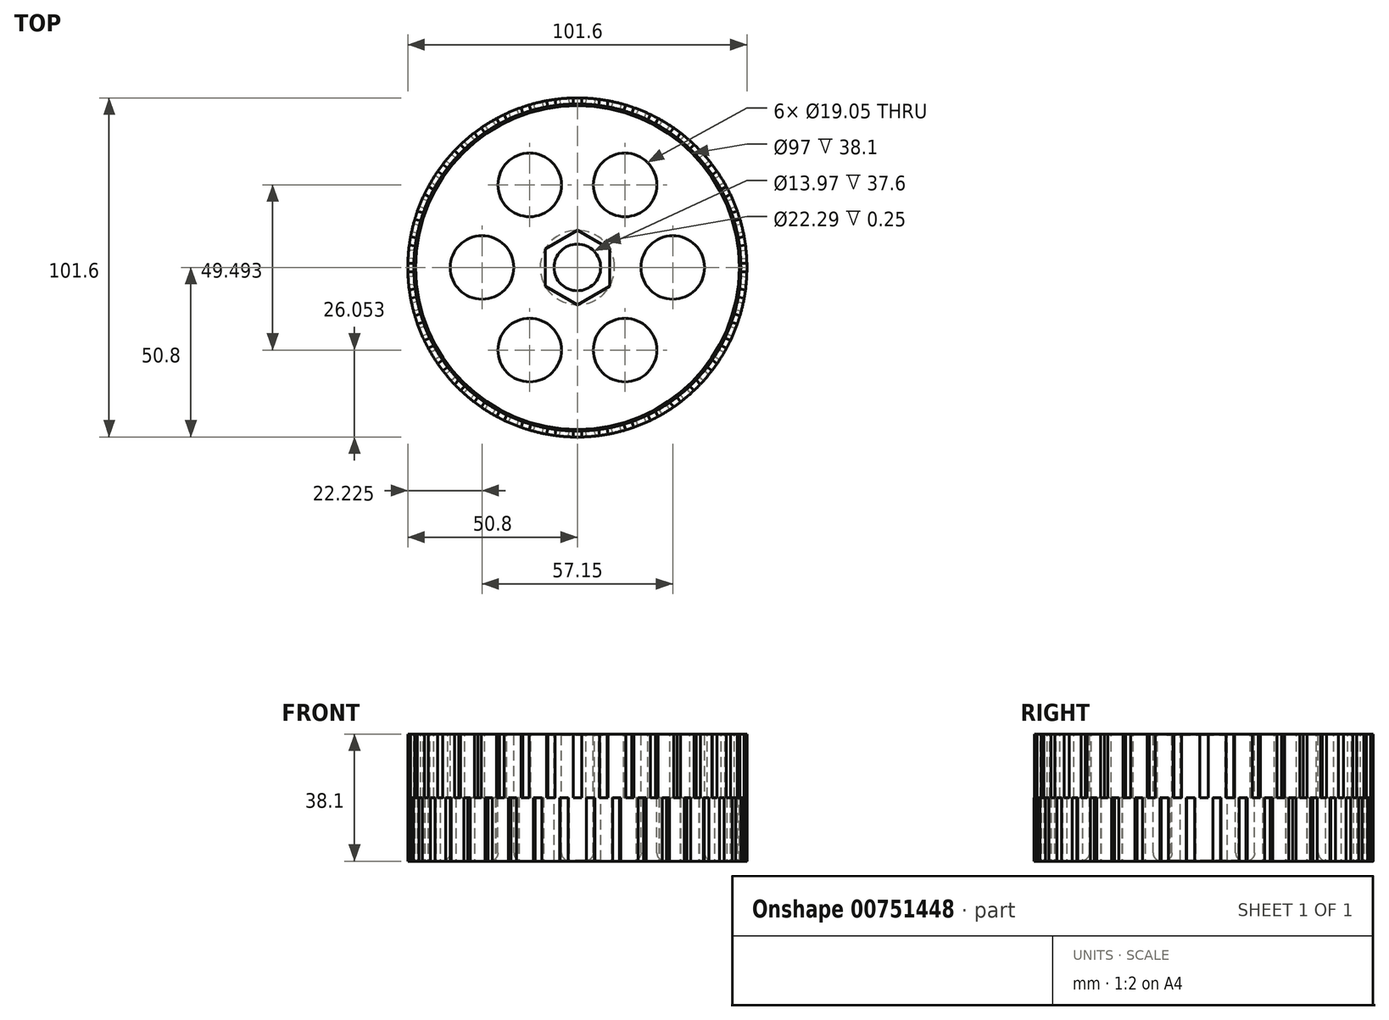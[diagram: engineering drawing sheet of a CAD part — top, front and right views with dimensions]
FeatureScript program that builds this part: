
annotation { "Feature Type Name" : "Feature", "Feature Type Description" : "" }
export const myFeature = defineFeature(function(context is Context, id is Id, definition is map)
    precondition{}
    {
        {
            assignVariable(context, id + "F0", {"name" : "BoltHeadDepth", "anyValue" : 0.25});
        }
        {
            assignVariable(context, id + "F1", {"name" : "NutDepth", "anyValue" : 0.25});
        }
        {
            var Q0;
            Q0=qCreatedBy(makeId("Front.planeOp"),FACE);
            var sketch = newSketch(context, id + "F2", { "sketchPlane" : qUnion([Q0])});
            skLineSegment(sketch, "E0.bottom", {"start": v(0, 38.1) * mm, "end": v(50.8, 38.1) * mm, "construction": true});
            skLineSegment(sketch, "E0.top", {"start": v(0, 0) * mm, "end": v(50.8, 0) * mm, "construction": true});
            skLineSegment(sketch, "E0.left", {"start": v(0, 38.1) * mm, "end": v(0, 0) * mm, "construction": true});
            skLineSegment(sketch, "E0.right", {"start": v(50.8, 38.1) * mm, "end": v(50.8, 0) * mm});
            skArc(sketch, "E1", {"start": v(49, 0) * mm, "mid": v(50.8, 19.05) * mm, "end": v(49, 38.1) * mm});
            skPoint(sketch, "E2", {"position": v(50.8, 19.05) * mm});
            skPoint(sketch, "E3", {"position": v(0, 19.05) * mm});
            skLineSegment(sketch, "E4.bottom", {"start": v(0, 38.1) * mm, "end": v(49, 38.1) * mm});
            skLineSegment(sketch, "E4.top", {"start": v(0, 0) * mm, "end": v(49, 0) * mm});
            skLineSegment(sketch, "E4.left", {"start": v(0, 38.1) * mm, "end": v(0, 0) * mm});
            skLineSegment(sketch, "E5", {"start": v(49, 38.1) * mm, "end": v(49, 0) * mm});
            skLineSegment(sketch, "E6.bottom", {"start": v(49, 38.1) * mm, "end": v(48, 38.1) * mm});
            skLineSegment(sketch, "E6.top", {"start": v(49, 0) * mm, "end": v(48, 0) * mm});
            skLineSegment(sketch, "E6.right", {"start": v(48, 38.1) * mm, "end": v(48, 0) * mm});
            skLineSegment(sketch, "E7", {"start": v(48.5, 38.1) * mm, "end": v(48.5, 0) * mm});
            skLineSegment(sketch, "E8", {"start": v(49, 38.1) * mm, "end": v(50.8, 38.1) * mm});
            skLineSegment(sketch, "E9", {"start": v(49, 0) * mm, "end": v(50.8, 0) * mm});
            skSolve(sketch);
        }
        {
            var Q0;
            Q0=makeQuery(id+"F2.imprint","IMPRINT",FACE,{"disambiguationData":[TD([[makeQuery(id+"F2.imprint","IMPRINT",EDGE,{"derivedFrom":sQuery(id+"F2.wireOp",EDGE,"E4.bottom")}),-1.0]])]});
            var Q1;
            {var subQ0=sQuery(id+"F2.wireOp",EDGE,"E6.right");Q1=makeQuery(id+"F2.imprint","IMPRINT",FACE,{"disambiguationData":[TD([[makeQuery(id+"F2.imprint","IMPRINT",EDGE,{"derivedFrom":subQ0}),1.0]])]});}
            var Q2;
            {var subQ0=sQuery(id+"F2.wireOp",EDGE,"E5");Q2=makeQuery(id+"F2.imprint","IMPRINT",FACE,{"disambiguationData":[TD([[makeQuery(id+"F2.imprint","IMPRINT",EDGE,{"derivedFrom":subQ0}),-1.0]])]});}
            var Q3;
            Q3=sQuery(id+"F2.wireOp",EDGE,"E4.left");
            revolve(context, id + "F3", {"surfaceOperationType" : NewSurfaceOperationType.NEW, "entities" : qUnion([Q0, Q1, Q2]), "axis" : qUnion([Q3]), "revolveType" : RevolveType.FULL});
        }
        {
            var Q0;
            Q0=makeQuery(id+"F2.imprint","IMPRINT",FACE,{"disambiguationData":[TD([[makeQuery(id+"F2.imprint","IMPRINT",EDGE,{"derivedFrom":sQuery(id+"F2.wireOp",EDGE,"E1")}),1.0]])]});
            var Q1;
            {var subQ0=sQuery(id+"F2.wireOp",EDGE,"E5");Q1=makeQuery(id+"F2.imprint","IMPRINT",FACE,{"disambiguationData":[TD([[makeQuery(id+"F2.imprint","IMPRINT",EDGE,{"derivedFrom":subQ0}),-1.0]])]});}
            var Q2;
            {var subQ0=sQuery(id+"F2.wireOp",EDGE,"E8");Q2=makeQuery(id+"F2.imprint","IMPRINT",FACE,{"disambiguationData":[TD([[makeQuery(id+"F2.imprint","IMPRINT",EDGE,{"derivedFrom":subQ0}),-1.0]])]});}
            var Q3;
            {var subQ0=sQuery(id+"F2.wireOp",EDGE,"E9");Q3=makeQuery(id+"F2.imprint","IMPRINT",FACE,{"disambiguationData":[TD([[makeQuery(id+"F2.imprint","IMPRINT",EDGE,{"derivedFrom":subQ0}),1.0]])]});}
            var Q4;
            Q4=sQuery(id+"F2.wireOp",EDGE,"E4.left");
            revolve(context, id + "F4", {"surfaceOperationType" : NewSurfaceOperationType.NEW, "entities" : qUnion([Q0, Q1, Q2, Q3]), "axis" : qUnion([Q4]), "revolveType" : RevolveType.FULL});
        }
        {
            var Q0;
            Q0=makeQuery(id+"F3.opRevolve","SWEPT_FACE",FACE,{"disambiguationData":[OSD([sQuery(id+"F2.wireOp",EDGE,"E4.bottom")])]});
            var sketch = newSketch(context, id + "F5", { "sketchPlane" : qUnion([Q0])});
            skCircle(sketch, "E10", {"center": v(0, 0) * mm, "radius": 6.99 * mm});
            skCircle(sketch, "E11.cCircle", {"center": v(0, 0) * mm, "radius": 9.65 * mm, "construction": true});
            skLineSegment(sketch, "E11.0", {"start": v(9.65, 5.57) * mm, "end": v(9.65, -5.57) * mm});
            skLineSegment(sketch, "E11.1", {"start": v(9.65, -5.57) * mm, "end": v(0, -11.15) * mm});
            skLineSegment(sketch, "E11.2", {"start": v(0, -11.15) * mm, "end": v(-9.65, -5.57) * mm});
            skLineSegment(sketch, "E11.3", {"start": v(-9.65, -5.57) * mm, "end": v(-9.65, 5.57) * mm});
            skLineSegment(sketch, "E11.4", {"start": v(-9.65, 5.57) * mm, "end": v(0, 11.15) * mm});
            skLineSegment(sketch, "E11.5", {"start": v(0, 11.15) * mm, "end": v(9.65, 5.57) * mm});
            skPoint(sketch, "E11.0.midPoint", {"position": v(9.65, 0) * mm});
            skSolve(sketch);
        }
        {
            var Q0;
            Q0=makeQuery(id+"F5.imprint","IMPRINT",FACE,{"disambiguationData":[TD([[makeQuery(id+"F5.imprint","IMPRINT",EDGE,{"derivedFrom":sQuery(id+"F5.wireOp",EDGE,"E10")}),1.0]])]});
            extrude(context, id + "F6", {"entities" : qUnion([Q0]), "operationType" : NewBodyOperationType.REMOVE, "endBound" : BoundingType.THROUGH_ALL, "oppositeDirection" : true, "depth" : 25.4 * mm, "offsetDistance" : 25.4 * mm});
        }
        {
            var Q0;
            Q0=makeQuery(id+"F5.imprint","IMPRINT",FACE,{"disambiguationData":[TD([[makeQuery(id+"F5.imprint","IMPRINT",EDGE,{"derivedFrom":sQuery(id+"F5.wireOp",EDGE,"E10")}),-1.0]])]});
            extrude(context, id + "F7", {"entities" : qUnion([Q0]), "operationType" : NewBodyOperationType.REMOVE, "oppositeDirection" : true, "depth" : (getVariable(context, 'BoltHeadDepth')) * mm, "offsetDistance" : 25.4 * mm});
        }
        {
            var Q0;
            Q0=makeQuery(id+"F3.opRevolve","SWEPT_FACE",FACE,{"disambiguationData":[OSD([sQuery(id+"F2.wireOp",EDGE,"E4.top")])]});
            var sketch = newSketch(context, id + "F8", { "sketchPlane" : qUnion([Q0])});
            skCircle(sketch, "E12", {"center": v(0, 0) * mm, "radius": 11.15 * mm});
            skSolve(sketch);
        }
        {
            var Q0;
            Q0=makeQuery(id+"F8.imprint","IMPRINT",FACE,{"disambiguationData":[TD([[makeQuery(id+"F8.imprint","IMPRINT",EDGE,{"derivedFrom":sQuery(id+"F8.wireOp",EDGE,"E12")}),1.0]])]});
            extrude(context, id + "F9", {"entities" : qUnion([Q0]), "operationType" : NewBodyOperationType.REMOVE, "oppositeDirection" : true, "depth" : (getVariable(context, 'NutDepth')) * mm, "offsetDistance" : 25.4 * mm});
        }
        {
            var Q0;
            Q0=makeQuery(id+"F5.imprint","IMPRINT",FACE,{"disambiguationData":[TD([[makeQuery(id+"F5.imprint","IMPRINT",EDGE,{"derivedFrom":sQuery(id+"F5.wireOp",EDGE,"E11.0")}),1.0]])]});
            var sketch = newSketch(context, id + "F10", { "sketchPlane" : qUnion([Q0])});
            skCircle(sketch, "E13", {"center": v(-28.58, 0) * mm, "radius": 9.53 * mm});
            skCircle(sketch, "E14", {"center": v(28.58, 0) * mm, "radius": 9.53 * mm});
            skCircle(sketch, "E15", {"center": v(0, 0) * mm, "radius": 28.58 * mm, "construction": true});
            skCircle(sketch, "E16.1.0", {"center": v(14.29, -24.75) * mm, "radius": 9.53 * mm});
            skCircle(sketch, "E16.1.1", {"center": v(-14.29, 24.75) * mm, "radius": 9.53 * mm});
            skCircle(sketch, "E16.2.0", {"center": v(14.29, 24.75) * mm, "radius": 9.53 * mm});
            skCircle(sketch, "E16.2.1", {"center": v(-14.29, -24.75) * mm, "radius": 9.53 * mm});
            skSolve(sketch);
        }
        {
            var Q0;
            Q0 = qSketchRegion(id + "F10", true);
            extrude(context, id + "F11", {"entities" : qUnion([Q0]), "operationType" : NewBodyOperationType.REMOVE, "endBound" : BoundingType.THROUGH_ALL, "oppositeDirection" : true, "depth" : 25.4 * mm, "offsetDistance" : 25.4 * mm});
        }
        {
            var Q0;
            Q0=makeQuery(id+"F11.boolean.opBoolean","COPY",EDGE,{"derivedFrom":makeQuery(id+"F11.opExtrude","CAP_EDGE",EDGE,{"disambiguationData":[OSD([sQuery(id+"F10.wireOp",EDGE,"E16.1.1")])],"isStart":true})});
            var Q1;
            Q1=makeQuery(id+"F11.boolean.opBoolean","COPY",EDGE,{"derivedFrom":makeQuery(id+"F11.opExtrude","CAP_EDGE",EDGE,{"disambiguationData":[OSD([sQuery(id+"F10.wireOp",EDGE,"E16.2.0")])],"isStart":true})});
            var Q2;
            Q2=makeQuery(id+"F11.boolean.opBoolean","COPY",EDGE,{"derivedFrom":makeQuery(id+"F11.opExtrude","CAP_EDGE",EDGE,{"disambiguationData":[OSD([sQuery(id+"F10.wireOp",EDGE,"E14")])],"isStart":true})});
            var Q3;
            Q3=makeQuery(id+"F11.boolean.opBoolean","COPY",EDGE,{"derivedFrom":makeQuery(id+"F11.opExtrude","CAP_EDGE",EDGE,{"disambiguationData":[OSD([sQuery(id+"F10.wireOp",EDGE,"E16.1.0")])],"isStart":true})});
            var Q4;
            Q4=makeQuery(id+"F11.boolean.opBoolean","COPY",EDGE,{"derivedFrom":makeQuery(id+"F11.opExtrude","CAP_EDGE",EDGE,{"disambiguationData":[OSD([sQuery(id+"F10.wireOp",EDGE,"E16.2.1")])],"isStart":true})});
            var Q5;
            Q5=makeQuery(id+"F11.boolean.opBoolean","COPY",EDGE,{"derivedFrom":makeQuery(id+"F11.opExtrude","CAP_EDGE",EDGE,{"disambiguationData":[OSD([sQuery(id+"F10.wireOp",EDGE,"E13")])],"isStart":true})});
            var Q6;
            Q6=makeQuery(id+"F11.boolean.opBoolean","INTERSECT",EDGE,{"derivedFrom":[makeQuery(id+"F3.opRevolve","SWEPT_FACE",FACE,{"disambiguationData":[OSD([sQuery(id+"F2.wireOp",EDGE,"E4.top"),sQuery(id+"F2.wireOp",EDGE,"E6.top")])]}),makeQuery(id+"F11.opExtrude","SWEPT_FACE",FACE,{"disambiguationData":[OSD([sQuery(id+"F10.wireOp",EDGE,"E16.1.1")])]})]});
            var Q7;
            Q7=makeQuery(id+"F11.boolean.opBoolean","INTERSECT",EDGE,{"derivedFrom":[makeQuery(id+"F3.opRevolve","SWEPT_FACE",FACE,{"disambiguationData":[OSD([sQuery(id+"F2.wireOp",EDGE,"E4.top"),sQuery(id+"F2.wireOp",EDGE,"E6.top")])]}),makeQuery(id+"F11.opExtrude","SWEPT_FACE",FACE,{"disambiguationData":[OSD([sQuery(id+"F10.wireOp",EDGE,"E13")])]})]});
            var Q8;
            Q8=makeQuery(id+"F11.boolean.opBoolean","INTERSECT",EDGE,{"derivedFrom":[makeQuery(id+"F3.opRevolve","SWEPT_FACE",FACE,{"disambiguationData":[OSD([sQuery(id+"F2.wireOp",EDGE,"E4.top"),sQuery(id+"F2.wireOp",EDGE,"E6.top")])]}),makeQuery(id+"F11.opExtrude","SWEPT_FACE",FACE,{"disambiguationData":[OSD([sQuery(id+"F10.wireOp",EDGE,"E16.2.1")])]})]});
            var Q9;
            Q9=makeQuery(id+"F11.boolean.opBoolean","INTERSECT",EDGE,{"derivedFrom":[makeQuery(id+"F3.opRevolve","SWEPT_FACE",FACE,{"disambiguationData":[OSD([sQuery(id+"F2.wireOp",EDGE,"E4.top"),sQuery(id+"F2.wireOp",EDGE,"E6.top")])]}),makeQuery(id+"F11.opExtrude","SWEPT_FACE",FACE,{"disambiguationData":[OSD([sQuery(id+"F10.wireOp",EDGE,"E16.1.0")])]})]});
            var Q10;
            Q10=makeQuery(id+"F11.boolean.opBoolean","INTERSECT",EDGE,{"derivedFrom":[makeQuery(id+"F3.opRevolve","SWEPT_FACE",FACE,{"disambiguationData":[OSD([sQuery(id+"F2.wireOp",EDGE,"E4.top"),sQuery(id+"F2.wireOp",EDGE,"E6.top")])]}),makeQuery(id+"F11.opExtrude","SWEPT_FACE",FACE,{"disambiguationData":[OSD([sQuery(id+"F10.wireOp",EDGE,"E14")])]})]});
            var Q11;
            Q11=makeQuery(id+"F11.boolean.opBoolean","INTERSECT",EDGE,{"derivedFrom":[makeQuery(id+"F3.opRevolve","SWEPT_FACE",FACE,{"disambiguationData":[OSD([sQuery(id+"F2.wireOp",EDGE,"E4.top"),sQuery(id+"F2.wireOp",EDGE,"E6.top")])]}),makeQuery(id+"F11.opExtrude","SWEPT_FACE",FACE,{"disambiguationData":[OSD([sQuery(id+"F10.wireOp",EDGE,"E16.2.0")])]})]});
            fillet(context, id + "F12", {"entities" : qUnion([Q0, Q1, Q2, Q3, Q4, Q5, Q6, Q7, Q8, Q9, Q10, Q11]), "radius" : 2.54 * mm, "tangentPropagation" : true, "allowEdgeOverflow" : false});
        }
        {
            var Q0;
            Q0=makeQuery(id+"F5.imprint","IMPRINT",FACE,{"disambiguationData":[TD([[makeQuery(id+"F5.imprint","IMPRINT",EDGE,{"derivedFrom":sQuery(id+"F5.wireOp",EDGE,"E11.0")}),1.0]])]});
            var sketch = newSketch(context, id + "F13", { "sketchPlane" : qUnion([Q0])});
            skLineSegment(sketch, "E17.bottom", {"start": v(-1.27, 51.52) * mm, "end": v(1.27, 51.52) * mm});
            skLineSegment(sketch, "E17.top", {"start": v(-1.27, 48.98) * mm, "end": v(1.27, 48.98) * mm});
            skLineSegment(sketch, "E17.left", {"start": v(-1.27, 51.52) * mm, "end": v(-1.27, 48.98) * mm});
            skLineSegment(sketch, "E17.right", {"start": v(1.27, 51.52) * mm, "end": v(1.27, 48.98) * mm});
            skPoint(sketch, "E18", {"position": v(0, 51.52) * mm});
            skPoint(sketch, "E18.positionSnap0", {"position": v(0, 51.52) * mm});
            skLineSegment(sketch, "E19.1.0", {"start": v(-6.8, 51.09) * mm, "end": v(-6.4, 48.58) * mm});
            skLineSegment(sketch, "E19.1.1", {"start": v(-9.31, 50.69) * mm, "end": v(-6.8, 51.09) * mm});
            skLineSegment(sketch, "E19.1.2", {"start": v(-9.31, 50.69) * mm, "end": v(-8.92, 48.18) * mm});
            skLineSegment(sketch, "E19.1.3", {"start": v(-8.92, 48.18) * mm, "end": v(-6.4, 48.58) * mm});
            skLineSegment(sketch, "E19.2.0", {"start": v(-14.71, 49.4) * mm, "end": v(-13.93, 46.98) * mm});
            skLineSegment(sketch, "E19.2.1", {"start": v(-17.13, 48.6) * mm, "end": v(-14.71, 49.4) * mm});
            skLineSegment(sketch, "E19.2.2", {"start": v(-17.13, 48.6) * mm, "end": v(-16.34, 46.2) * mm});
            skLineSegment(sketch, "E19.2.3", {"start": v(-16.34, 46.2) * mm, "end": v(-13.93, 46.98) * mm});
            skLineSegment(sketch, "E19.3.0", {"start": v(-22.26, 46.48) * mm, "end": v(-21.1, 44.22) * mm});
            skLineSegment(sketch, "E19.3.1", {"start": v(-24.52, 45.33) * mm, "end": v(-22.26, 46.48) * mm});
            skLineSegment(sketch, "E19.3.2", {"start": v(-24.52, 45.33) * mm, "end": v(-23.37, 43.07) * mm});
            skLineSegment(sketch, "E19.3.3", {"start": v(-23.37, 43.07) * mm, "end": v(-21.1, 44.22) * mm});
            skLineSegment(sketch, "E19.4.0", {"start": v(-29.26, 42.43) * mm, "end": v(-27.76, 40.37) * mm});
            skLineSegment(sketch, "E19.4.1", {"start": v(-31.31, 40.94) * mm, "end": v(-29.26, 42.43) * mm});
            skLineSegment(sketch, "E19.4.2", {"start": v(-31.31, 40.94) * mm, "end": v(-29.82, 38.88) * mm});
            skLineSegment(sketch, "E19.4.3", {"start": v(-29.82, 38.88) * mm, "end": v(-27.76, 40.37) * mm});
            skLineSegment(sketch, "E19.5.0", {"start": v(-35.53, 37.33) * mm, "end": v(-33.74, 35.53) * mm});
            skLineSegment(sketch, "E19.5.1", {"start": v(-37.33, 35.53) * mm, "end": v(-35.53, 37.33) * mm});
            skLineSegment(sketch, "E19.5.2", {"start": v(-37.33, 35.53) * mm, "end": v(-35.53, 33.74) * mm});
            skLineSegment(sketch, "E19.5.3", {"start": v(-35.53, 33.74) * mm, "end": v(-33.74, 35.53) * mm});
            skLineSegment(sketch, "E19.6.0", {"start": v(-40.94, 31.31) * mm, "end": v(-38.88, 29.82) * mm});
            skLineSegment(sketch, "E19.6.1", {"start": v(-42.43, 29.26) * mm, "end": v(-40.94, 31.31) * mm});
            skLineSegment(sketch, "E19.6.2", {"start": v(-42.43, 29.26) * mm, "end": v(-40.37, 27.76) * mm});
            skLineSegment(sketch, "E19.6.3", {"start": v(-40.37, 27.76) * mm, "end": v(-38.88, 29.82) * mm});
            skLineSegment(sketch, "E19.7.0", {"start": v(-45.33, 24.52) * mm, "end": v(-43.07, 23.37) * mm});
            skLineSegment(sketch, "E19.7.1", {"start": v(-46.48, 22.26) * mm, "end": v(-45.33, 24.52) * mm});
            skLineSegment(sketch, "E19.7.2", {"start": v(-46.48, 22.26) * mm, "end": v(-44.22, 21.1) * mm});
            skLineSegment(sketch, "E19.7.3", {"start": v(-44.22, 21.1) * mm, "end": v(-43.07, 23.37) * mm});
            skLineSegment(sketch, "E19.8.0", {"start": v(-48.6, 17.13) * mm, "end": v(-46.2, 16.34) * mm});
            skLineSegment(sketch, "E19.8.1", {"start": v(-49.4, 14.71) * mm, "end": v(-48.6, 17.13) * mm});
            skLineSegment(sketch, "E19.8.2", {"start": v(-49.4, 14.71) * mm, "end": v(-46.98, 13.93) * mm});
            skLineSegment(sketch, "E19.8.3", {"start": v(-46.98, 13.93) * mm, "end": v(-46.2, 16.34) * mm});
            skLineSegment(sketch, "E19.9.0", {"start": v(-50.69, 9.31) * mm, "end": v(-48.18, 8.92) * mm});
            skLineSegment(sketch, "E19.9.1", {"start": v(-51.09, 6.8) * mm, "end": v(-50.69, 9.31) * mm});
            skLineSegment(sketch, "E19.9.2", {"start": v(-51.09, 6.8) * mm, "end": v(-48.58, 6.4) * mm});
            skLineSegment(sketch, "E19.9.3", {"start": v(-48.58, 6.4) * mm, "end": v(-48.18, 8.92) * mm});
            skLineSegment(sketch, "E19.10.0", {"start": v(-51.52, 1.27) * mm, "end": v(-48.98, 1.27) * mm});
            skLineSegment(sketch, "E19.10.1", {"start": v(-51.52, -1.27) * mm, "end": v(-51.52, 1.27) * mm});
            skLineSegment(sketch, "E19.10.2", {"start": v(-51.52, -1.27) * mm, "end": v(-48.98, -1.27) * mm});
            skLineSegment(sketch, "E19.10.3", {"start": v(-48.98, -1.27) * mm, "end": v(-48.98, 1.27) * mm});
            skLineSegment(sketch, "E19.11.0", {"start": v(-51.09, -6.8) * mm, "end": v(-48.58, -6.4) * mm});
            skLineSegment(sketch, "E19.11.1", {"start": v(-50.69, -9.31) * mm, "end": v(-51.09, -6.8) * mm});
            skLineSegment(sketch, "E19.11.2", {"start": v(-50.69, -9.31) * mm, "end": v(-48.18, -8.92) * mm});
            skLineSegment(sketch, "E19.11.3", {"start": v(-48.18, -8.92) * mm, "end": v(-48.58, -6.4) * mm});
            skLineSegment(sketch, "E19.12.0", {"start": v(-49.4, -14.71) * mm, "end": v(-46.98, -13.93) * mm});
            skLineSegment(sketch, "E19.12.1", {"start": v(-48.6, -17.13) * mm, "end": v(-49.4, -14.71) * mm});
            skLineSegment(sketch, "E19.12.2", {"start": v(-48.6, -17.13) * mm, "end": v(-46.2, -16.34) * mm});
            skLineSegment(sketch, "E19.12.3", {"start": v(-46.2, -16.34) * mm, "end": v(-46.98, -13.93) * mm});
            skLineSegment(sketch, "E19.13.0", {"start": v(-46.48, -22.26) * mm, "end": v(-44.22, -21.1) * mm});
            skLineSegment(sketch, "E19.13.1", {"start": v(-45.33, -24.52) * mm, "end": v(-46.48, -22.26) * mm});
            skLineSegment(sketch, "E19.13.2", {"start": v(-45.33, -24.52) * mm, "end": v(-43.07, -23.37) * mm});
            skLineSegment(sketch, "E19.13.3", {"start": v(-43.07, -23.37) * mm, "end": v(-44.22, -21.1) * mm});
            skLineSegment(sketch, "E19.14.0", {"start": v(-42.43, -29.26) * mm, "end": v(-40.37, -27.76) * mm});
            skLineSegment(sketch, "E19.14.1", {"start": v(-40.94, -31.31) * mm, "end": v(-42.43, -29.26) * mm});
            skLineSegment(sketch, "E19.14.2", {"start": v(-40.94, -31.31) * mm, "end": v(-38.88, -29.82) * mm});
            skLineSegment(sketch, "E19.14.3", {"start": v(-38.88, -29.82) * mm, "end": v(-40.37, -27.76) * mm});
            skLineSegment(sketch, "E19.15.0", {"start": v(-37.33, -35.53) * mm, "end": v(-35.53, -33.74) * mm});
            skLineSegment(sketch, "E19.15.1", {"start": v(-35.53, -37.33) * mm, "end": v(-37.33, -35.53) * mm});
            skLineSegment(sketch, "E19.15.2", {"start": v(-35.53, -37.33) * mm, "end": v(-33.74, -35.53) * mm});
            skLineSegment(sketch, "E19.15.3", {"start": v(-33.74, -35.53) * mm, "end": v(-35.53, -33.74) * mm});
            skLineSegment(sketch, "E19.16.0", {"start": v(-31.31, -40.94) * mm, "end": v(-29.82, -38.88) * mm});
            skLineSegment(sketch, "E19.16.1", {"start": v(-29.26, -42.43) * mm, "end": v(-31.31, -40.94) * mm});
            skLineSegment(sketch, "E19.16.2", {"start": v(-29.26, -42.43) * mm, "end": v(-27.76, -40.37) * mm});
            skLineSegment(sketch, "E19.16.3", {"start": v(-27.76, -40.37) * mm, "end": v(-29.82, -38.88) * mm});
            skLineSegment(sketch, "E19.17.0", {"start": v(-24.52, -45.33) * mm, "end": v(-23.37, -43.07) * mm});
            skLineSegment(sketch, "E19.17.1", {"start": v(-22.26, -46.48) * mm, "end": v(-24.52, -45.33) * mm});
            skLineSegment(sketch, "E19.17.2", {"start": v(-22.26, -46.48) * mm, "end": v(-21.1, -44.22) * mm});
            skLineSegment(sketch, "E19.17.3", {"start": v(-21.1, -44.22) * mm, "end": v(-23.37, -43.07) * mm});
            skLineSegment(sketch, "E19.18.0", {"start": v(-17.13, -48.6) * mm, "end": v(-16.34, -46.2) * mm});
            skLineSegment(sketch, "E19.18.1", {"start": v(-14.71, -49.4) * mm, "end": v(-17.13, -48.6) * mm});
            skLineSegment(sketch, "E19.18.2", {"start": v(-14.71, -49.4) * mm, "end": v(-13.93, -46.98) * mm});
            skLineSegment(sketch, "E19.18.3", {"start": v(-13.93, -46.98) * mm, "end": v(-16.34, -46.2) * mm});
            skLineSegment(sketch, "E19.19.0", {"start": v(-9.31, -50.69) * mm, "end": v(-8.92, -48.18) * mm});
            skLineSegment(sketch, "E19.19.1", {"start": v(-6.8, -51.09) * mm, "end": v(-9.31, -50.69) * mm});
            skLineSegment(sketch, "E19.19.2", {"start": v(-6.8, -51.09) * mm, "end": v(-6.4, -48.58) * mm});
            skLineSegment(sketch, "E19.19.3", {"start": v(-6.4, -48.58) * mm, "end": v(-8.92, -48.18) * mm});
            skLineSegment(sketch, "E19.20.0", {"start": v(-1.27, -51.52) * mm, "end": v(-1.27, -48.98) * mm});
            skLineSegment(sketch, "E19.20.1", {"start": v(1.27, -51.52) * mm, "end": v(-1.27, -51.52) * mm});
            skLineSegment(sketch, "E19.20.2", {"start": v(1.27, -51.52) * mm, "end": v(1.27, -48.98) * mm});
            skLineSegment(sketch, "E19.20.3", {"start": v(1.27, -48.98) * mm, "end": v(-1.27, -48.98) * mm});
            skLineSegment(sketch, "E19.21.0", {"start": v(6.8, -51.09) * mm, "end": v(6.4, -48.58) * mm});
            skLineSegment(sketch, "E19.21.1", {"start": v(9.31, -50.69) * mm, "end": v(6.8, -51.09) * mm});
            skLineSegment(sketch, "E19.21.2", {"start": v(9.31, -50.69) * mm, "end": v(8.92, -48.18) * mm});
            skLineSegment(sketch, "E19.21.3", {"start": v(8.92, -48.18) * mm, "end": v(6.4, -48.58) * mm});
            skLineSegment(sketch, "E19.22.0", {"start": v(14.71, -49.4) * mm, "end": v(13.93, -46.98) * mm});
            skLineSegment(sketch, "E19.22.1", {"start": v(17.13, -48.6) * mm, "end": v(14.71, -49.4) * mm});
            skLineSegment(sketch, "E19.22.2", {"start": v(17.13, -48.6) * mm, "end": v(16.34, -46.2) * mm});
            skLineSegment(sketch, "E19.22.3", {"start": v(16.34, -46.2) * mm, "end": v(13.93, -46.98) * mm});
            skLineSegment(sketch, "E19.23.0", {"start": v(22.26, -46.48) * mm, "end": v(21.1, -44.22) * mm});
            skLineSegment(sketch, "E19.23.1", {"start": v(24.52, -45.33) * mm, "end": v(22.26, -46.48) * mm});
            skLineSegment(sketch, "E19.23.2", {"start": v(24.52, -45.33) * mm, "end": v(23.37, -43.07) * mm});
            skLineSegment(sketch, "E19.23.3", {"start": v(23.37, -43.07) * mm, "end": v(21.1, -44.22) * mm});
            skLineSegment(sketch, "E19.24.0", {"start": v(29.26, -42.43) * mm, "end": v(27.76, -40.37) * mm});
            skLineSegment(sketch, "E19.24.1", {"start": v(31.31, -40.94) * mm, "end": v(29.26, -42.43) * mm});
            skLineSegment(sketch, "E19.24.2", {"start": v(31.31, -40.94) * mm, "end": v(29.82, -38.88) * mm});
            skLineSegment(sketch, "E19.24.3", {"start": v(29.82, -38.88) * mm, "end": v(27.76, -40.37) * mm});
            skLineSegment(sketch, "E19.25.0", {"start": v(35.53, -37.33) * mm, "end": v(33.74, -35.53) * mm});
            skLineSegment(sketch, "E19.25.1", {"start": v(37.33, -35.53) * mm, "end": v(35.53, -37.33) * mm});
            skLineSegment(sketch, "E19.25.2", {"start": v(37.33, -35.53) * mm, "end": v(35.53, -33.74) * mm});
            skLineSegment(sketch, "E19.25.3", {"start": v(35.53, -33.74) * mm, "end": v(33.74, -35.53) * mm});
            skLineSegment(sketch, "E19.26.0", {"start": v(40.94, -31.31) * mm, "end": v(38.88, -29.82) * mm});
            skLineSegment(sketch, "E19.26.1", {"start": v(42.43, -29.26) * mm, "end": v(40.94, -31.31) * mm});
            skLineSegment(sketch, "E19.26.2", {"start": v(42.43, -29.26) * mm, "end": v(40.37, -27.76) * mm});
            skLineSegment(sketch, "E19.26.3", {"start": v(40.37, -27.76) * mm, "end": v(38.88, -29.82) * mm});
            skLineSegment(sketch, "E19.27.0", {"start": v(45.33, -24.52) * mm, "end": v(43.07, -23.37) * mm});
            skLineSegment(sketch, "E19.27.1", {"start": v(46.48, -22.26) * mm, "end": v(45.33, -24.52) * mm});
            skLineSegment(sketch, "E19.27.2", {"start": v(46.48, -22.26) * mm, "end": v(44.22, -21.1) * mm});
            skLineSegment(sketch, "E19.27.3", {"start": v(44.22, -21.1) * mm, "end": v(43.07, -23.37) * mm});
            skLineSegment(sketch, "E19.28.0", {"start": v(48.6, -17.13) * mm, "end": v(46.2, -16.34) * mm});
            skLineSegment(sketch, "E19.28.1", {"start": v(49.4, -14.71) * mm, "end": v(48.6, -17.13) * mm});
            skLineSegment(sketch, "E19.28.2", {"start": v(49.4, -14.71) * mm, "end": v(46.98, -13.93) * mm});
            skLineSegment(sketch, "E19.28.3", {"start": v(46.98, -13.93) * mm, "end": v(46.2, -16.34) * mm});
            skLineSegment(sketch, "E19.29.0", {"start": v(50.69, -9.31) * mm, "end": v(48.18, -8.92) * mm});
            skLineSegment(sketch, "E19.29.1", {"start": v(51.09, -6.8) * mm, "end": v(50.69, -9.31) * mm});
            skLineSegment(sketch, "E19.29.2", {"start": v(51.09, -6.8) * mm, "end": v(48.58, -6.4) * mm});
            skLineSegment(sketch, "E19.29.3", {"start": v(48.58, -6.4) * mm, "end": v(48.18, -8.92) * mm});
            skLineSegment(sketch, "E19.30.0", {"start": v(51.52, -1.27) * mm, "end": v(48.98, -1.27) * mm});
            skLineSegment(sketch, "E19.30.1", {"start": v(51.52, 1.27) * mm, "end": v(51.52, -1.27) * mm});
            skLineSegment(sketch, "E19.30.2", {"start": v(51.52, 1.27) * mm, "end": v(48.98, 1.27) * mm});
            skLineSegment(sketch, "E19.30.3", {"start": v(48.98, 1.27) * mm, "end": v(48.98, -1.27) * mm});
            skLineSegment(sketch, "E19.31.0", {"start": v(51.09, 6.8) * mm, "end": v(48.58, 6.4) * mm});
            skLineSegment(sketch, "E19.31.1", {"start": v(50.69, 9.31) * mm, "end": v(51.09, 6.8) * mm});
            skLineSegment(sketch, "E19.31.2", {"start": v(50.69, 9.31) * mm, "end": v(48.18, 8.92) * mm});
            skLineSegment(sketch, "E19.31.3", {"start": v(48.18, 8.92) * mm, "end": v(48.58, 6.4) * mm});
            skLineSegment(sketch, "E19.32.0", {"start": v(49.4, 14.71) * mm, "end": v(46.98, 13.93) * mm});
            skLineSegment(sketch, "E19.32.1", {"start": v(48.6, 17.13) * mm, "end": v(49.4, 14.71) * mm});
            skLineSegment(sketch, "E19.32.2", {"start": v(48.6, 17.13) * mm, "end": v(46.2, 16.34) * mm});
            skLineSegment(sketch, "E19.32.3", {"start": v(46.2, 16.34) * mm, "end": v(46.98, 13.93) * mm});
            skLineSegment(sketch, "E19.33.0", {"start": v(46.48, 22.26) * mm, "end": v(44.22, 21.1) * mm});
            skLineSegment(sketch, "E19.33.1", {"start": v(45.33, 24.52) * mm, "end": v(46.48, 22.26) * mm});
            skLineSegment(sketch, "E19.33.2", {"start": v(45.33, 24.52) * mm, "end": v(43.07, 23.37) * mm});
            skLineSegment(sketch, "E19.33.3", {"start": v(43.07, 23.37) * mm, "end": v(44.22, 21.1) * mm});
            skLineSegment(sketch, "E19.34.0", {"start": v(42.43, 29.26) * mm, "end": v(40.37, 27.76) * mm});
            skLineSegment(sketch, "E19.34.1", {"start": v(40.94, 31.31) * mm, "end": v(42.43, 29.26) * mm});
            skLineSegment(sketch, "E19.34.2", {"start": v(40.94, 31.31) * mm, "end": v(38.88, 29.82) * mm});
            skLineSegment(sketch, "E19.34.3", {"start": v(38.88, 29.82) * mm, "end": v(40.37, 27.76) * mm});
            skLineSegment(sketch, "E19.35.0", {"start": v(37.33, 35.53) * mm, "end": v(35.53, 33.74) * mm});
            skLineSegment(sketch, "E19.35.1", {"start": v(35.53, 37.33) * mm, "end": v(37.33, 35.53) * mm});
            skLineSegment(sketch, "E19.35.2", {"start": v(35.53, 37.33) * mm, "end": v(33.74, 35.53) * mm});
            skLineSegment(sketch, "E19.35.3", {"start": v(33.74, 35.53) * mm, "end": v(35.53, 33.74) * mm});
            skLineSegment(sketch, "E19.36.0", {"start": v(31.31, 40.94) * mm, "end": v(29.82, 38.88) * mm});
            skLineSegment(sketch, "E19.36.1", {"start": v(29.26, 42.43) * mm, "end": v(31.31, 40.94) * mm});
            skLineSegment(sketch, "E19.36.2", {"start": v(29.26, 42.43) * mm, "end": v(27.76, 40.37) * mm});
            skLineSegment(sketch, "E19.36.3", {"start": v(27.76, 40.37) * mm, "end": v(29.82, 38.88) * mm});
            skLineSegment(sketch, "E19.37.0", {"start": v(24.52, 45.33) * mm, "end": v(23.37, 43.07) * mm});
            skLineSegment(sketch, "E19.37.1", {"start": v(22.26, 46.48) * mm, "end": v(24.52, 45.33) * mm});
            skLineSegment(sketch, "E19.37.2", {"start": v(22.26, 46.48) * mm, "end": v(21.1, 44.22) * mm});
            skLineSegment(sketch, "E19.37.3", {"start": v(21.1, 44.22) * mm, "end": v(23.37, 43.07) * mm});
            skLineSegment(sketch, "E19.38.0", {"start": v(17.13, 48.6) * mm, "end": v(16.34, 46.2) * mm});
            skLineSegment(sketch, "E19.38.1", {"start": v(14.71, 49.4) * mm, "end": v(17.13, 48.6) * mm});
            skLineSegment(sketch, "E19.38.2", {"start": v(14.71, 49.4) * mm, "end": v(13.93, 46.98) * mm});
            skLineSegment(sketch, "E19.38.3", {"start": v(13.93, 46.98) * mm, "end": v(16.34, 46.2) * mm});
            skLineSegment(sketch, "E19.39.0", {"start": v(9.31, 50.69) * mm, "end": v(8.92, 48.18) * mm});
            skLineSegment(sketch, "E19.39.1", {"start": v(6.8, 51.09) * mm, "end": v(9.31, 50.69) * mm});
            skLineSegment(sketch, "E19.39.2", {"start": v(6.8, 51.09) * mm, "end": v(6.4, 48.58) * mm});
            skLineSegment(sketch, "E19.39.3", {"start": v(6.4, 48.58) * mm, "end": v(8.92, 48.18) * mm});
            skPoint(sketch, "E19.center", {"position": v(0, 0) * mm});
            skLineSegment(sketch, "E20", {"start": v(2.74, 51.46) * mm, "end": v(2.54, 48.93) * mm});
            skLineSegment(sketch, "E21", {"start": v(2.54, 48.93) * mm, "end": v(5.07, 48.73) * mm});
            skLineSegment(sketch, "E22", {"start": v(5.07, 48.73) * mm, "end": v(5.27, 51.27) * mm});
            skLineSegment(sketch, "E23", {"start": v(5.27, 51.27) * mm, "end": v(2.74, 51.46) * mm});
            skSolve(sketch);
        }
        {
            var Q0;
            Q0=makeQuery(id+"F13.imprint","IMPRINT",FACE,{"disambiguationData":[TD([[makeQuery(id+"F13.imprint","IMPRINT",EDGE,{"derivedFrom":sQuery(id+"F13.wireOp",EDGE,"E17.bottom")}),-1.0]])]});
            var Q1;
            {var subQ0=sQuery(id+"F13.wireOp",EDGE,"E19.1.0");Q1=makeQuery(id+"F13.imprint","IMPRINT",FACE,{"disambiguationData":[TD([[makeQuery(id+"F13.imprint","IMPRINT",EDGE,{"derivedFrom":subQ0}),-1.0]])]});}
            var Q2;
            {var subQ0=sQuery(id+"F13.wireOp",EDGE,"E19.2.0");Q2=makeQuery(id+"F13.imprint","IMPRINT",FACE,{"disambiguationData":[TD([[makeQuery(id+"F13.imprint","IMPRINT",EDGE,{"derivedFrom":subQ0}),-1.0]])]});}
            var Q3;
            {var subQ0=sQuery(id+"F13.wireOp",EDGE,"E19.3.0");Q3=makeQuery(id+"F13.imprint","IMPRINT",FACE,{"disambiguationData":[TD([[makeQuery(id+"F13.imprint","IMPRINT",EDGE,{"derivedFrom":subQ0}),-1.0]])]});}
            var Q4;
            {var subQ0=sQuery(id+"F13.wireOp",EDGE,"E19.4.0");Q4=makeQuery(id+"F13.imprint","IMPRINT",FACE,{"disambiguationData":[TD([[makeQuery(id+"F13.imprint","IMPRINT",EDGE,{"derivedFrom":subQ0}),-1.0]])]});}
            var Q5;
            {var subQ0=sQuery(id+"F13.wireOp",EDGE,"E19.5.0");Q5=makeQuery(id+"F13.imprint","IMPRINT",FACE,{"disambiguationData":[TD([[makeQuery(id+"F13.imprint","IMPRINT",EDGE,{"derivedFrom":subQ0}),-1.0]])]});}
            var Q6;
            {var subQ0=sQuery(id+"F13.wireOp",EDGE,"E19.6.0");Q6=makeQuery(id+"F13.imprint","IMPRINT",FACE,{"disambiguationData":[TD([[makeQuery(id+"F13.imprint","IMPRINT",EDGE,{"derivedFrom":subQ0}),-1.0]])]});}
            var Q7;
            {var subQ0=sQuery(id+"F13.wireOp",EDGE,"E19.7.0");Q7=makeQuery(id+"F13.imprint","IMPRINT",FACE,{"disambiguationData":[TD([[makeQuery(id+"F13.imprint","IMPRINT",EDGE,{"derivedFrom":subQ0}),-1.0]])]});}
            var Q8;
            {var subQ0=sQuery(id+"F13.wireOp",EDGE,"E19.8.0");Q8=makeQuery(id+"F13.imprint","IMPRINT",FACE,{"disambiguationData":[TD([[makeQuery(id+"F13.imprint","IMPRINT",EDGE,{"derivedFrom":subQ0}),-1.0]])]});}
            var Q9;
            {var subQ0=sQuery(id+"F13.wireOp",EDGE,"E19.9.0");Q9=makeQuery(id+"F13.imprint","IMPRINT",FACE,{"disambiguationData":[TD([[makeQuery(id+"F13.imprint","IMPRINT",EDGE,{"derivedFrom":subQ0}),-1.0]])]});}
            var Q10;
            {var subQ0=sQuery(id+"F13.wireOp",EDGE,"E19.10.0");Q10=makeQuery(id+"F13.imprint","IMPRINT",FACE,{"disambiguationData":[TD([[makeQuery(id+"F13.imprint","IMPRINT",EDGE,{"derivedFrom":subQ0}),-1.0]])]});}
            var Q11;
            {var subQ0=sQuery(id+"F13.wireOp",EDGE,"E19.11.0");Q11=makeQuery(id+"F13.imprint","IMPRINT",FACE,{"disambiguationData":[TD([[makeQuery(id+"F13.imprint","IMPRINT",EDGE,{"derivedFrom":subQ0}),-1.0]])]});}
            var Q12;
            {var subQ0=sQuery(id+"F13.wireOp",EDGE,"E19.12.0");Q12=makeQuery(id+"F13.imprint","IMPRINT",FACE,{"disambiguationData":[TD([[makeQuery(id+"F13.imprint","IMPRINT",EDGE,{"derivedFrom":subQ0}),-1.0]])]});}
            var Q13;
            {var subQ0=sQuery(id+"F13.wireOp",EDGE,"E19.13.0");Q13=makeQuery(id+"F13.imprint","IMPRINT",FACE,{"disambiguationData":[TD([[makeQuery(id+"F13.imprint","IMPRINT",EDGE,{"derivedFrom":subQ0}),-1.0]])]});}
            var Q14;
            {var subQ0=sQuery(id+"F13.wireOp",EDGE,"E19.14.0");Q14=makeQuery(id+"F13.imprint","IMPRINT",FACE,{"disambiguationData":[TD([[makeQuery(id+"F13.imprint","IMPRINT",EDGE,{"derivedFrom":subQ0}),-1.0]])]});}
            var Q15;
            {var subQ0=sQuery(id+"F13.wireOp",EDGE,"E19.15.0");Q15=makeQuery(id+"F13.imprint","IMPRINT",FACE,{"disambiguationData":[TD([[makeQuery(id+"F13.imprint","IMPRINT",EDGE,{"derivedFrom":subQ0}),-1.0]])]});}
            var Q16;
            {var subQ0=sQuery(id+"F13.wireOp",EDGE,"E19.16.0");Q16=makeQuery(id+"F13.imprint","IMPRINT",FACE,{"disambiguationData":[TD([[makeQuery(id+"F13.imprint","IMPRINT",EDGE,{"derivedFrom":subQ0}),-1.0]])]});}
            var Q17;
            {var subQ0=sQuery(id+"F13.wireOp",EDGE,"E19.17.0");Q17=makeQuery(id+"F13.imprint","IMPRINT",FACE,{"disambiguationData":[TD([[makeQuery(id+"F13.imprint","IMPRINT",EDGE,{"derivedFrom":subQ0}),-1.0]])]});}
            var Q18;
            {var subQ0=sQuery(id+"F13.wireOp",EDGE,"E19.18.0");Q18=makeQuery(id+"F13.imprint","IMPRINT",FACE,{"disambiguationData":[TD([[makeQuery(id+"F13.imprint","IMPRINT",EDGE,{"derivedFrom":subQ0}),-1.0]])]});}
            var Q19;
            {var subQ0=sQuery(id+"F13.wireOp",EDGE,"E19.19.0");Q19=makeQuery(id+"F13.imprint","IMPRINT",FACE,{"disambiguationData":[TD([[makeQuery(id+"F13.imprint","IMPRINT",EDGE,{"derivedFrom":subQ0}),-1.0]])]});}
            var Q20;
            {var subQ0=sQuery(id+"F13.wireOp",EDGE,"E19.20.0");Q20=makeQuery(id+"F13.imprint","IMPRINT",FACE,{"disambiguationData":[TD([[makeQuery(id+"F13.imprint","IMPRINT",EDGE,{"derivedFrom":subQ0}),-1.0]])]});}
            var Q21;
            {var subQ0=sQuery(id+"F13.wireOp",EDGE,"E19.21.0");Q21=makeQuery(id+"F13.imprint","IMPRINT",FACE,{"disambiguationData":[TD([[makeQuery(id+"F13.imprint","IMPRINT",EDGE,{"derivedFrom":subQ0}),-1.0]])]});}
            var Q22;
            {var subQ0=sQuery(id+"F13.wireOp",EDGE,"E19.22.0");Q22=makeQuery(id+"F13.imprint","IMPRINT",FACE,{"disambiguationData":[TD([[makeQuery(id+"F13.imprint","IMPRINT",EDGE,{"derivedFrom":subQ0}),-1.0]])]});}
            var Q23;
            {var subQ0=sQuery(id+"F13.wireOp",EDGE,"E19.23.0");Q23=makeQuery(id+"F13.imprint","IMPRINT",FACE,{"disambiguationData":[TD([[makeQuery(id+"F13.imprint","IMPRINT",EDGE,{"derivedFrom":subQ0}),-1.0]])]});}
            var Q24;
            {var subQ0=sQuery(id+"F13.wireOp",EDGE,"E19.24.0");Q24=makeQuery(id+"F13.imprint","IMPRINT",FACE,{"disambiguationData":[TD([[makeQuery(id+"F13.imprint","IMPRINT",EDGE,{"derivedFrom":subQ0}),-1.0]])]});}
            var Q25;
            {var subQ0=sQuery(id+"F13.wireOp",EDGE,"E19.25.0");Q25=makeQuery(id+"F13.imprint","IMPRINT",FACE,{"disambiguationData":[TD([[makeQuery(id+"F13.imprint","IMPRINT",EDGE,{"derivedFrom":subQ0}),-1.0]])]});}
            var Q26;
            {var subQ0=sQuery(id+"F13.wireOp",EDGE,"E19.26.0");Q26=makeQuery(id+"F13.imprint","IMPRINT",FACE,{"disambiguationData":[TD([[makeQuery(id+"F13.imprint","IMPRINT",EDGE,{"derivedFrom":subQ0}),-1.0]])]});}
            var Q27;
            {var subQ0=sQuery(id+"F13.wireOp",EDGE,"E19.27.0");Q27=makeQuery(id+"F13.imprint","IMPRINT",FACE,{"disambiguationData":[TD([[makeQuery(id+"F13.imprint","IMPRINT",EDGE,{"derivedFrom":subQ0}),-1.0]])]});}
            var Q28;
            {var subQ0=sQuery(id+"F13.wireOp",EDGE,"E19.28.0");Q28=makeQuery(id+"F13.imprint","IMPRINT",FACE,{"disambiguationData":[TD([[makeQuery(id+"F13.imprint","IMPRINT",EDGE,{"derivedFrom":subQ0}),-1.0]])]});}
            var Q29;
            {var subQ0=sQuery(id+"F13.wireOp",EDGE,"E19.29.0");Q29=makeQuery(id+"F13.imprint","IMPRINT",FACE,{"disambiguationData":[TD([[makeQuery(id+"F13.imprint","IMPRINT",EDGE,{"derivedFrom":subQ0}),-1.0]])]});}
            var Q30;
            {var subQ0=sQuery(id+"F13.wireOp",EDGE,"E19.30.0");Q30=makeQuery(id+"F13.imprint","IMPRINT",FACE,{"disambiguationData":[TD([[makeQuery(id+"F13.imprint","IMPRINT",EDGE,{"derivedFrom":subQ0}),-1.0]])]});}
            var Q31;
            {var subQ0=sQuery(id+"F13.wireOp",EDGE,"E19.31.0");Q31=makeQuery(id+"F13.imprint","IMPRINT",FACE,{"disambiguationData":[TD([[makeQuery(id+"F13.imprint","IMPRINT",EDGE,{"derivedFrom":subQ0}),-1.0]])]});}
            var Q32;
            {var subQ0=sQuery(id+"F13.wireOp",EDGE,"E19.32.0");Q32=makeQuery(id+"F13.imprint","IMPRINT",FACE,{"disambiguationData":[TD([[makeQuery(id+"F13.imprint","IMPRINT",EDGE,{"derivedFrom":subQ0}),-1.0]])]});}
            var Q33;
            {var subQ0=sQuery(id+"F13.wireOp",EDGE,"E19.33.0");Q33=makeQuery(id+"F13.imprint","IMPRINT",FACE,{"disambiguationData":[TD([[makeQuery(id+"F13.imprint","IMPRINT",EDGE,{"derivedFrom":subQ0}),-1.0]])]});}
            var Q34;
            {var subQ0=sQuery(id+"F13.wireOp",EDGE,"E19.34.0");Q34=makeQuery(id+"F13.imprint","IMPRINT",FACE,{"disambiguationData":[TD([[makeQuery(id+"F13.imprint","IMPRINT",EDGE,{"derivedFrom":subQ0}),-1.0]])]});}
            var Q35;
            {var subQ0=sQuery(id+"F13.wireOp",EDGE,"E19.35.0");Q35=makeQuery(id+"F13.imprint","IMPRINT",FACE,{"disambiguationData":[TD([[makeQuery(id+"F13.imprint","IMPRINT",EDGE,{"derivedFrom":subQ0}),-1.0]])]});}
            var Q36;
            {var subQ0=sQuery(id+"F13.wireOp",EDGE,"E19.36.0");Q36=makeQuery(id+"F13.imprint","IMPRINT",FACE,{"disambiguationData":[TD([[makeQuery(id+"F13.imprint","IMPRINT",EDGE,{"derivedFrom":subQ0}),-1.0]])]});}
            var Q37;
            {var subQ0=sQuery(id+"F13.wireOp",EDGE,"E19.37.0");Q37=makeQuery(id+"F13.imprint","IMPRINT",FACE,{"disambiguationData":[TD([[makeQuery(id+"F13.imprint","IMPRINT",EDGE,{"derivedFrom":subQ0}),-1.0]])]});}
            var Q38;
            {var subQ0=sQuery(id+"F13.wireOp",EDGE,"E19.38.0");Q38=makeQuery(id+"F13.imprint","IMPRINT",FACE,{"disambiguationData":[TD([[makeQuery(id+"F13.imprint","IMPRINT",EDGE,{"derivedFrom":subQ0}),-1.0]])]});}
            var Q39;
            {var subQ0=sQuery(id+"F13.wireOp",EDGE,"E19.39.0");Q39=makeQuery(id+"F13.imprint","IMPRINT",FACE,{"disambiguationData":[TD([[makeQuery(id+"F13.imprint","IMPRINT",EDGE,{"derivedFrom":subQ0}),-1.0]])]});}
            var Q40;
            {var subQ0=sQuery(id+"F13.wireOp",EDGE,"E17.top");Q40=makeQuery(id+"F13.imprint","IMPRINT",FACE,{"disambiguationData":[TD([[makeQuery(id+"F13.imprint","IMPRINT",EDGE,{"derivedFrom":subQ0}),1.0]])]});}
            var Q41;
            {var subQ0=sQuery(id+"F13.wireOp",EDGE,"E19.1.3");Q41=makeQuery(id+"F13.imprint","IMPRINT",FACE,{"disambiguationData":[TD([[makeQuery(id+"F13.imprint","IMPRINT",EDGE,{"derivedFrom":subQ0}),1.0]])]});}
            var Q42;
            {var subQ0=sQuery(id+"F13.wireOp",EDGE,"E19.2.3");Q42=makeQuery(id+"F13.imprint","IMPRINT",FACE,{"disambiguationData":[TD([[makeQuery(id+"F13.imprint","IMPRINT",EDGE,{"derivedFrom":subQ0}),1.0]])]});}
            var Q43;
            {var subQ0=sQuery(id+"F13.wireOp",EDGE,"E19.3.3");Q43=makeQuery(id+"F13.imprint","IMPRINT",FACE,{"disambiguationData":[TD([[makeQuery(id+"F13.imprint","IMPRINT",EDGE,{"derivedFrom":subQ0}),1.0]])]});}
            var Q44;
            {var subQ0=sQuery(id+"F13.wireOp",EDGE,"E19.4.3");Q44=makeQuery(id+"F13.imprint","IMPRINT",FACE,{"disambiguationData":[TD([[makeQuery(id+"F13.imprint","IMPRINT",EDGE,{"derivedFrom":subQ0}),1.0]])]});}
            var Q45;
            {var subQ0=sQuery(id+"F13.wireOp",EDGE,"E19.5.3");Q45=makeQuery(id+"F13.imprint","IMPRINT",FACE,{"disambiguationData":[TD([[makeQuery(id+"F13.imprint","IMPRINT",EDGE,{"derivedFrom":subQ0}),1.0]])]});}
            var Q46;
            {var subQ0=sQuery(id+"F13.wireOp",EDGE,"E19.6.3");Q46=makeQuery(id+"F13.imprint","IMPRINT",FACE,{"disambiguationData":[TD([[makeQuery(id+"F13.imprint","IMPRINT",EDGE,{"derivedFrom":subQ0}),1.0]])]});}
            var Q47;
            {var subQ0=sQuery(id+"F13.wireOp",EDGE,"E19.7.3");Q47=makeQuery(id+"F13.imprint","IMPRINT",FACE,{"disambiguationData":[TD([[makeQuery(id+"F13.imprint","IMPRINT",EDGE,{"derivedFrom":subQ0}),1.0]])]});}
            var Q48;
            {var subQ0=sQuery(id+"F13.wireOp",EDGE,"E19.8.3");Q48=makeQuery(id+"F13.imprint","IMPRINT",FACE,{"disambiguationData":[TD([[makeQuery(id+"F13.imprint","IMPRINT",EDGE,{"derivedFrom":subQ0}),1.0]])]});}
            var Q49;
            {var subQ0=sQuery(id+"F13.wireOp",EDGE,"E19.9.3");Q49=makeQuery(id+"F13.imprint","IMPRINT",FACE,{"disambiguationData":[TD([[makeQuery(id+"F13.imprint","IMPRINT",EDGE,{"derivedFrom":subQ0}),1.0]])]});}
            var Q50;
            {var subQ0=sQuery(id+"F13.wireOp",EDGE,"E19.10.3");Q50=makeQuery(id+"F13.imprint","IMPRINT",FACE,{"disambiguationData":[TD([[makeQuery(id+"F13.imprint","IMPRINT",EDGE,{"derivedFrom":subQ0}),1.0]])]});}
            var Q51;
            {var subQ0=sQuery(id+"F13.wireOp",EDGE,"E19.11.3");Q51=makeQuery(id+"F13.imprint","IMPRINT",FACE,{"disambiguationData":[TD([[makeQuery(id+"F13.imprint","IMPRINT",EDGE,{"derivedFrom":subQ0}),1.0]])]});}
            var Q52;
            {var subQ0=sQuery(id+"F13.wireOp",EDGE,"E19.12.3");Q52=makeQuery(id+"F13.imprint","IMPRINT",FACE,{"disambiguationData":[TD([[makeQuery(id+"F13.imprint","IMPRINT",EDGE,{"derivedFrom":subQ0}),1.0]])]});}
            var Q53;
            {var subQ0=sQuery(id+"F13.wireOp",EDGE,"E19.13.3");Q53=makeQuery(id+"F13.imprint","IMPRINT",FACE,{"disambiguationData":[TD([[makeQuery(id+"F13.imprint","IMPRINT",EDGE,{"derivedFrom":subQ0}),1.0]])]});}
            var Q54;
            {var subQ0=sQuery(id+"F13.wireOp",EDGE,"E19.14.3");Q54=makeQuery(id+"F13.imprint","IMPRINT",FACE,{"disambiguationData":[TD([[makeQuery(id+"F13.imprint","IMPRINT",EDGE,{"derivedFrom":subQ0}),1.0]])]});}
            var Q55;
            {var subQ0=sQuery(id+"F13.wireOp",EDGE,"E19.15.3");Q55=makeQuery(id+"F13.imprint","IMPRINT",FACE,{"disambiguationData":[TD([[makeQuery(id+"F13.imprint","IMPRINT",EDGE,{"derivedFrom":subQ0}),1.0]])]});}
            var Q56;
            {var subQ0=sQuery(id+"F13.wireOp",EDGE,"E19.16.3");Q56=makeQuery(id+"F13.imprint","IMPRINT",FACE,{"disambiguationData":[TD([[makeQuery(id+"F13.imprint","IMPRINT",EDGE,{"derivedFrom":subQ0}),1.0]])]});}
            var Q57;
            {var subQ0=sQuery(id+"F13.wireOp",EDGE,"E19.17.3");Q57=makeQuery(id+"F13.imprint","IMPRINT",FACE,{"disambiguationData":[TD([[makeQuery(id+"F13.imprint","IMPRINT",EDGE,{"derivedFrom":subQ0}),1.0]])]});}
            var Q58;
            {var subQ0=sQuery(id+"F13.wireOp",EDGE,"E19.18.3");Q58=makeQuery(id+"F13.imprint","IMPRINT",FACE,{"disambiguationData":[TD([[makeQuery(id+"F13.imprint","IMPRINT",EDGE,{"derivedFrom":subQ0}),1.0]])]});}
            var Q59;
            {var subQ0=sQuery(id+"F13.wireOp",EDGE,"E19.19.3");Q59=makeQuery(id+"F13.imprint","IMPRINT",FACE,{"disambiguationData":[TD([[makeQuery(id+"F13.imprint","IMPRINT",EDGE,{"derivedFrom":subQ0}),1.0]])]});}
            var Q60;
            {var subQ0=sQuery(id+"F13.wireOp",EDGE,"E19.20.3");Q60=makeQuery(id+"F13.imprint","IMPRINT",FACE,{"disambiguationData":[TD([[makeQuery(id+"F13.imprint","IMPRINT",EDGE,{"derivedFrom":subQ0}),1.0]])]});}
            var Q61;
            {var subQ0=sQuery(id+"F13.wireOp",EDGE,"E19.21.3");Q61=makeQuery(id+"F13.imprint","IMPRINT",FACE,{"disambiguationData":[TD([[makeQuery(id+"F13.imprint","IMPRINT",EDGE,{"derivedFrom":subQ0}),1.0]])]});}
            var Q62;
            {var subQ0=sQuery(id+"F13.wireOp",EDGE,"E19.22.3");Q62=makeQuery(id+"F13.imprint","IMPRINT",FACE,{"disambiguationData":[TD([[makeQuery(id+"F13.imprint","IMPRINT",EDGE,{"derivedFrom":subQ0}),1.0]])]});}
            var Q63;
            {var subQ0=sQuery(id+"F13.wireOp",EDGE,"E19.23.3");Q63=makeQuery(id+"F13.imprint","IMPRINT",FACE,{"disambiguationData":[TD([[makeQuery(id+"F13.imprint","IMPRINT",EDGE,{"derivedFrom":subQ0}),1.0]])]});}
            var Q64;
            {var subQ0=sQuery(id+"F13.wireOp",EDGE,"E19.24.3");Q64=makeQuery(id+"F13.imprint","IMPRINT",FACE,{"disambiguationData":[TD([[makeQuery(id+"F13.imprint","IMPRINT",EDGE,{"derivedFrom":subQ0}),1.0]])]});}
            var Q65;
            {var subQ0=sQuery(id+"F13.wireOp",EDGE,"E19.25.3");Q65=makeQuery(id+"F13.imprint","IMPRINT",FACE,{"disambiguationData":[TD([[makeQuery(id+"F13.imprint","IMPRINT",EDGE,{"derivedFrom":subQ0}),1.0]])]});}
            var Q66;
            {var subQ0=sQuery(id+"F13.wireOp",EDGE,"E19.26.3");Q66=makeQuery(id+"F13.imprint","IMPRINT",FACE,{"disambiguationData":[TD([[makeQuery(id+"F13.imprint","IMPRINT",EDGE,{"derivedFrom":subQ0}),1.0]])]});}
            var Q67;
            {var subQ0=sQuery(id+"F13.wireOp",EDGE,"E19.27.3");Q67=makeQuery(id+"F13.imprint","IMPRINT",FACE,{"disambiguationData":[TD([[makeQuery(id+"F13.imprint","IMPRINT",EDGE,{"derivedFrom":subQ0}),1.0]])]});}
            var Q68;
            {var subQ0=sQuery(id+"F13.wireOp",EDGE,"E19.28.3");Q68=makeQuery(id+"F13.imprint","IMPRINT",FACE,{"disambiguationData":[TD([[makeQuery(id+"F13.imprint","IMPRINT",EDGE,{"derivedFrom":subQ0}),1.0]])]});}
            var Q69;
            {var subQ0=sQuery(id+"F13.wireOp",EDGE,"E19.29.3");Q69=makeQuery(id+"F13.imprint","IMPRINT",FACE,{"disambiguationData":[TD([[makeQuery(id+"F13.imprint","IMPRINT",EDGE,{"derivedFrom":subQ0}),1.0]])]});}
            var Q70;
            {var subQ0=sQuery(id+"F13.wireOp",EDGE,"E19.30.3");Q70=makeQuery(id+"F13.imprint","IMPRINT",FACE,{"disambiguationData":[TD([[makeQuery(id+"F13.imprint","IMPRINT",EDGE,{"derivedFrom":subQ0}),1.0]])]});}
            var Q71;
            {var subQ0=sQuery(id+"F13.wireOp",EDGE,"E19.31.3");Q71=makeQuery(id+"F13.imprint","IMPRINT",FACE,{"disambiguationData":[TD([[makeQuery(id+"F13.imprint","IMPRINT",EDGE,{"derivedFrom":subQ0}),1.0]])]});}
            var Q72;
            {var subQ0=sQuery(id+"F13.wireOp",EDGE,"E19.32.3");Q72=makeQuery(id+"F13.imprint","IMPRINT",FACE,{"disambiguationData":[TD([[makeQuery(id+"F13.imprint","IMPRINT",EDGE,{"derivedFrom":subQ0}),1.0]])]});}
            var Q73;
            {var subQ0=sQuery(id+"F13.wireOp",EDGE,"E19.33.3");Q73=makeQuery(id+"F13.imprint","IMPRINT",FACE,{"disambiguationData":[TD([[makeQuery(id+"F13.imprint","IMPRINT",EDGE,{"derivedFrom":subQ0}),1.0]])]});}
            var Q74;
            {var subQ0=sQuery(id+"F13.wireOp",EDGE,"E19.34.3");Q74=makeQuery(id+"F13.imprint","IMPRINT",FACE,{"disambiguationData":[TD([[makeQuery(id+"F13.imprint","IMPRINT",EDGE,{"derivedFrom":subQ0}),1.0]])]});}
            var Q75;
            {var subQ0=sQuery(id+"F13.wireOp",EDGE,"E19.35.3");Q75=makeQuery(id+"F13.imprint","IMPRINT",FACE,{"disambiguationData":[TD([[makeQuery(id+"F13.imprint","IMPRINT",EDGE,{"derivedFrom":subQ0}),1.0]])]});}
            var Q76;
            {var subQ0=sQuery(id+"F13.wireOp",EDGE,"E19.36.3");Q76=makeQuery(id+"F13.imprint","IMPRINT",FACE,{"disambiguationData":[TD([[makeQuery(id+"F13.imprint","IMPRINT",EDGE,{"derivedFrom":subQ0}),1.0]])]});}
            var Q77;
            {var subQ0=sQuery(id+"F13.wireOp",EDGE,"E19.37.3");Q77=makeQuery(id+"F13.imprint","IMPRINT",FACE,{"disambiguationData":[TD([[makeQuery(id+"F13.imprint","IMPRINT",EDGE,{"derivedFrom":subQ0}),1.0]])]});}
            var Q78;
            {var subQ0=sQuery(id+"F13.wireOp",EDGE,"E19.38.3");Q78=makeQuery(id+"F13.imprint","IMPRINT",FACE,{"disambiguationData":[TD([[makeQuery(id+"F13.imprint","IMPRINT",EDGE,{"derivedFrom":subQ0}),1.0]])]});}
            var Q79;
            {var subQ0=sQuery(id+"F13.wireOp",EDGE,"E19.39.3");Q79=makeQuery(id+"F13.imprint","IMPRINT",FACE,{"disambiguationData":[TD([[makeQuery(id+"F13.imprint","IMPRINT",EDGE,{"derivedFrom":subQ0}),1.0]])]});}
            var Q80;
            {var subQ0=sQuery(id+"F13.wireOp",EDGE,"E21");Q80=makeQuery(id+"F13.imprint","IMPRINT",FACE,{"disambiguationData":[TD([[makeQuery(id+"F13.imprint","IMPRINT",EDGE,{"derivedFrom":subQ0}),1.0]])]});}
            var Q81;
            Q81=makeQuery(id+"F3.opRevolve","SWEPT_FACE",FACE,{"disambiguationData":[OSD([sQuery(id+"F2.wireOp",EDGE,"E4.top"),sQuery(id+"F2.wireOp",EDGE,"E6.top")])]});
            extrude(context, id + "F14", {"entities" : qUnion([Q0, Q1, Q2, Q3, Q4, Q5, Q6, Q7, Q8, Q9, Q10, Q11, Q12, Q13, Q14, Q15, Q16, Q17, Q18, Q19, Q20, Q21, Q22, Q23, Q24, Q25, Q26, Q27, Q28, Q29, Q30, Q31, Q32, Q33, Q34, Q35, Q36, Q37, Q38, Q39, Q40, Q41, Q42, Q43, Q44, Q45, Q46, Q47, Q48, Q49, Q50, Q51, Q52, Q53, Q54, Q55, Q56, Q57, Q58, Q59, Q60, Q61, Q62, Q63, Q64, Q65, Q66, Q67, Q68, Q69, Q70, Q71, Q72, Q73, Q74, Q75, Q76, Q77, Q78, Q79, Q80, Q81]), "operationType" : NewBodyOperationType.REMOVE, "oppositeDirection" : true, "depth" : 19.05 * mm, "offsetDistance" : 25.4 * mm});
        }
        {
            var Q0;
            Q0=makeQuery(id+"F3.opRevolve","SWEPT_FACE",FACE,{"disambiguationData":[OSD([sQuery(id+"F2.wireOp",EDGE,"E4.top"),sQuery(id+"F2.wireOp",EDGE,"E6.top")])]});
            var sketch = newSketch(context, id + "F15", { "sketchPlane" : qUnion([Q0])});
            skPoint(sketch, "E24.center", {"position": v(-0.05, -0.05) * mm});
            skLineSegment(sketch, "E25", {"start": v(2.74, 51.46) * mm, "end": v(2.54, 48.93) * mm});
            skLineSegment(sketch, "E26", {"start": v(2.54, 48.93) * mm, "end": v(5.07, 48.73) * mm});
            skLineSegment(sketch, "E27", {"start": v(5.07, 48.73) * mm, "end": v(5.27, 51.27) * mm});
            skLineSegment(sketch, "E28", {"start": v(5.27, 51.27) * mm, "end": v(2.74, 51.46) * mm});
            skLineSegment(sketch, "E29.1.0", {"start": v(-5.15, 48.73) * mm, "end": v(-2.61, 48.93) * mm});
            skLineSegment(sketch, "E29.1.1", {"start": v(-5.35, 51.26) * mm, "end": v(-5.15, 48.73) * mm});
            skLineSegment(sketch, "E29.1.2", {"start": v(-2.82, 51.46) * mm, "end": v(-5.35, 51.26) * mm});
            skLineSegment(sketch, "E29.1.3", {"start": v(-2.61, 48.93) * mm, "end": v(-2.82, 51.46) * mm});
            skLineSegment(sketch, "E29.2.0", {"start": v(-12.7, 47.32) * mm, "end": v(-10.24, 47.92) * mm});
            skLineSegment(sketch, "E29.2.1", {"start": v(-13.3, 49.8) * mm, "end": v(-12.7, 47.32) * mm});
            skLineSegment(sketch, "E29.2.2", {"start": v(-10.83, 50.39) * mm, "end": v(-13.3, 49.8) * mm});
            skLineSegment(sketch, "E29.2.3", {"start": v(-10.24, 47.92) * mm, "end": v(-10.83, 50.39) * mm});
            skLineSegment(sketch, "E29.3.0", {"start": v(-19.95, 44.75) * mm, "end": v(-17.6, 45.73) * mm});
            skLineSegment(sketch, "E29.3.1", {"start": v(-20.93, 47.1) * mm, "end": v(-19.95, 44.75) * mm});
            skLineSegment(sketch, "E29.3.2", {"start": v(-18.58, 48.07) * mm, "end": v(-20.93, 47.1) * mm});
            skLineSegment(sketch, "E29.3.3", {"start": v(-17.6, 45.73) * mm, "end": v(-18.58, 48.07) * mm});
            skLineSegment(sketch, "E29.4.0", {"start": v(-26.7, 41.08) * mm, "end": v(-24.54, 42.4) * mm});
            skLineSegment(sketch, "E29.4.1", {"start": v(-28.04, 43.24) * mm, "end": v(-26.7, 41.08) * mm});
            skLineSegment(sketch, "E29.4.2", {"start": v(-25.87, 44.57) * mm, "end": v(-28.04, 43.24) * mm});
            skLineSegment(sketch, "E29.4.3", {"start": v(-24.54, 42.4) * mm, "end": v(-25.87, 44.57) * mm});
            skLineSegment(sketch, "E29.5.0", {"start": v(-32.8, 36.4) * mm, "end": v(-30.87, 38.05) * mm});
            skLineSegment(sketch, "E29.5.1", {"start": v(-34.46, 38.33) * mm, "end": v(-32.8, 36.4) * mm});
            skLineSegment(sketch, "E29.5.2", {"start": v(-32.53, 39.98) * mm, "end": v(-34.46, 38.33) * mm});
            skLineSegment(sketch, "E29.5.3", {"start": v(-30.87, 38.05) * mm, "end": v(-32.53, 39.98) * mm});
            skLineSegment(sketch, "E29.6.0", {"start": v(-38.1, 30.82) * mm, "end": v(-36.45, 32.75) * mm});
            skLineSegment(sketch, "E29.6.1", {"start": v(-40.03, 32.46) * mm, "end": v(-38.1, 30.82) * mm});
            skLineSegment(sketch, "E29.6.2", {"start": v(-38.38, 34.4) * mm, "end": v(-40.03, 32.46) * mm});
            skLineSegment(sketch, "E29.6.3", {"start": v(-36.45, 32.75) * mm, "end": v(-38.38, 34.4) * mm});
            skLineSegment(sketch, "E29.7.0", {"start": v(-42.45, 24.48) * mm, "end": v(-41.12, 26.64) * mm});
            skLineSegment(sketch, "E29.7.1", {"start": v(-44.61, 25.8) * mm, "end": v(-42.45, 24.48) * mm});
            skLineSegment(sketch, "E29.7.2", {"start": v(-43.29, 27.97) * mm, "end": v(-44.61, 25.8) * mm});
            skLineSegment(sketch, "E29.7.3", {"start": v(-41.12, 26.64) * mm, "end": v(-43.29, 27.97) * mm});
            skLineSegment(sketch, "E29.8.0", {"start": v(-45.75, 17.54) * mm, "end": v(-44.78, 19.88) * mm});
            skLineSegment(sketch, "E29.8.1", {"start": v(-48.1, 18.5) * mm, "end": v(-45.75, 17.54) * mm});
            skLineSegment(sketch, "E29.8.2", {"start": v(-47.13, 20.85) * mm, "end": v(-48.1, 18.5) * mm});
            skLineSegment(sketch, "E29.8.3", {"start": v(-44.78, 19.88) * mm, "end": v(-47.13, 20.85) * mm});
            skLineSegment(sketch, "E29.9.0", {"start": v(-47.93, 10.16) * mm, "end": v(-47.34, 12.63) * mm});
            skLineSegment(sketch, "E29.9.1", {"start": v(-50.4, 10.75) * mm, "end": v(-47.93, 10.16) * mm});
            skLineSegment(sketch, "E29.9.2", {"start": v(-49.81, 13.22) * mm, "end": v(-50.4, 10.75) * mm});
            skLineSegment(sketch, "E29.9.3", {"start": v(-47.34, 12.63) * mm, "end": v(-49.81, 13.22) * mm});
            skLineSegment(sketch, "E29.10.0", {"start": v(-48.93, 2.54) * mm, "end": v(-48.73, 5.07) * mm});
            skLineSegment(sketch, "E29.10.1", {"start": v(-51.46, 2.74) * mm, "end": v(-48.93, 2.54) * mm});
            skLineSegment(sketch, "E29.10.2", {"start": v(-51.27, 5.27) * mm, "end": v(-51.46, 2.74) * mm});
            skLineSegment(sketch, "E29.10.3", {"start": v(-48.73, 5.07) * mm, "end": v(-51.27, 5.27) * mm});
            skLineSegment(sketch, "E29.11.0", {"start": v(-48.73, -5.15) * mm, "end": v(-48.93, -2.61) * mm});
            skLineSegment(sketch, "E29.11.1", {"start": v(-51.26, -5.35) * mm, "end": v(-48.73, -5.15) * mm});
            skLineSegment(sketch, "E29.11.2", {"start": v(-51.46, -2.82) * mm, "end": v(-51.26, -5.35) * mm});
            skLineSegment(sketch, "E29.11.3", {"start": v(-48.93, -2.61) * mm, "end": v(-51.46, -2.82) * mm});
            skLineSegment(sketch, "E29.12.0", {"start": v(-47.32, -12.7) * mm, "end": v(-47.92, -10.24) * mm});
            skLineSegment(sketch, "E29.12.1", {"start": v(-49.8, -13.3) * mm, "end": v(-47.32, -12.7) * mm});
            skLineSegment(sketch, "E29.12.2", {"start": v(-50.39, -10.83) * mm, "end": v(-49.8, -13.3) * mm});
            skLineSegment(sketch, "E29.12.3", {"start": v(-47.92, -10.24) * mm, "end": v(-50.39, -10.83) * mm});
            skLineSegment(sketch, "E29.13.0", {"start": v(-44.75, -19.95) * mm, "end": v(-45.73, -17.6) * mm});
            skLineSegment(sketch, "E29.13.1", {"start": v(-47.1, -20.93) * mm, "end": v(-44.75, -19.95) * mm});
            skLineSegment(sketch, "E29.13.2", {"start": v(-48.07, -18.58) * mm, "end": v(-47.1, -20.93) * mm});
            skLineSegment(sketch, "E29.13.3", {"start": v(-45.73, -17.6) * mm, "end": v(-48.07, -18.58) * mm});
            skLineSegment(sketch, "E29.14.0", {"start": v(-41.08, -26.7) * mm, "end": v(-42.4, -24.54) * mm});
            skLineSegment(sketch, "E29.14.1", {"start": v(-43.24, -28.04) * mm, "end": v(-41.08, -26.7) * mm});
            skLineSegment(sketch, "E29.14.2", {"start": v(-44.57, -25.87) * mm, "end": v(-43.24, -28.04) * mm});
            skLineSegment(sketch, "E29.14.3", {"start": v(-42.4, -24.54) * mm, "end": v(-44.57, -25.87) * mm});
            skLineSegment(sketch, "E29.15.0", {"start": v(-36.4, -32.8) * mm, "end": v(-38.05, -30.87) * mm});
            skLineSegment(sketch, "E29.15.1", {"start": v(-38.33, -34.46) * mm, "end": v(-36.4, -32.8) * mm});
            skLineSegment(sketch, "E29.15.2", {"start": v(-39.98, -32.53) * mm, "end": v(-38.33, -34.46) * mm});
            skLineSegment(sketch, "E29.15.3", {"start": v(-38.05, -30.87) * mm, "end": v(-39.98, -32.53) * mm});
            skLineSegment(sketch, "E29.16.0", {"start": v(-30.82, -38.1) * mm, "end": v(-32.75, -36.45) * mm});
            skLineSegment(sketch, "E29.16.1", {"start": v(-32.46, -40.03) * mm, "end": v(-30.82, -38.1) * mm});
            skLineSegment(sketch, "E29.16.2", {"start": v(-34.4, -38.38) * mm, "end": v(-32.46, -40.03) * mm});
            skLineSegment(sketch, "E29.16.3", {"start": v(-32.75, -36.45) * mm, "end": v(-34.4, -38.38) * mm});
            skLineSegment(sketch, "E29.17.0", {"start": v(-24.48, -42.45) * mm, "end": v(-26.64, -41.12) * mm});
            skLineSegment(sketch, "E29.17.1", {"start": v(-25.8, -44.61) * mm, "end": v(-24.48, -42.45) * mm});
            skLineSegment(sketch, "E29.17.2", {"start": v(-27.97, -43.29) * mm, "end": v(-25.8, -44.61) * mm});
            skLineSegment(sketch, "E29.17.3", {"start": v(-26.64, -41.12) * mm, "end": v(-27.97, -43.29) * mm});
            skLineSegment(sketch, "E29.18.0", {"start": v(-17.54, -45.75) * mm, "end": v(-19.88, -44.78) * mm});
            skLineSegment(sketch, "E29.18.1", {"start": v(-18.5, -48.1) * mm, "end": v(-17.54, -45.75) * mm});
            skLineSegment(sketch, "E29.18.2", {"start": v(-20.85, -47.13) * mm, "end": v(-18.5, -48.1) * mm});
            skLineSegment(sketch, "E29.18.3", {"start": v(-19.88, -44.78) * mm, "end": v(-20.85, -47.13) * mm});
            skLineSegment(sketch, "E29.19.0", {"start": v(-10.16, -47.93) * mm, "end": v(-12.63, -47.34) * mm});
            skLineSegment(sketch, "E29.19.1", {"start": v(-10.75, -50.4) * mm, "end": v(-10.16, -47.93) * mm});
            skLineSegment(sketch, "E29.19.2", {"start": v(-13.22, -49.81) * mm, "end": v(-10.75, -50.4) * mm});
            skLineSegment(sketch, "E29.19.3", {"start": v(-12.63, -47.34) * mm, "end": v(-13.22, -49.81) * mm});
            skLineSegment(sketch, "E29.20.0", {"start": v(-2.54, -48.93) * mm, "end": v(-5.07, -48.73) * mm});
            skLineSegment(sketch, "E29.20.1", {"start": v(-2.74, -51.46) * mm, "end": v(-2.54, -48.93) * mm});
            skLineSegment(sketch, "E29.20.2", {"start": v(-5.27, -51.27) * mm, "end": v(-2.74, -51.46) * mm});
            skLineSegment(sketch, "E29.20.3", {"start": v(-5.07, -48.73) * mm, "end": v(-5.27, -51.27) * mm});
            skLineSegment(sketch, "E29.21.0", {"start": v(5.15, -48.73) * mm, "end": v(2.61, -48.93) * mm});
            skLineSegment(sketch, "E29.21.1", {"start": v(5.35, -51.26) * mm, "end": v(5.15, -48.73) * mm});
            skLineSegment(sketch, "E29.21.2", {"start": v(2.82, -51.46) * mm, "end": v(5.35, -51.26) * mm});
            skLineSegment(sketch, "E29.21.3", {"start": v(2.61, -48.93) * mm, "end": v(2.82, -51.46) * mm});
            skLineSegment(sketch, "E29.22.0", {"start": v(12.7, -47.32) * mm, "end": v(10.24, -47.92) * mm});
            skLineSegment(sketch, "E29.22.1", {"start": v(13.3, -49.8) * mm, "end": v(12.7, -47.32) * mm});
            skLineSegment(sketch, "E29.22.2", {"start": v(10.83, -50.39) * mm, "end": v(13.3, -49.8) * mm});
            skLineSegment(sketch, "E29.22.3", {"start": v(10.24, -47.92) * mm, "end": v(10.83, -50.39) * mm});
            skLineSegment(sketch, "E29.23.0", {"start": v(19.95, -44.75) * mm, "end": v(17.6, -45.73) * mm});
            skLineSegment(sketch, "E29.23.1", {"start": v(20.93, -47.1) * mm, "end": v(19.95, -44.75) * mm});
            skLineSegment(sketch, "E29.23.2", {"start": v(18.58, -48.07) * mm, "end": v(20.93, -47.1) * mm});
            skLineSegment(sketch, "E29.23.3", {"start": v(17.6, -45.73) * mm, "end": v(18.58, -48.07) * mm});
            skLineSegment(sketch, "E29.24.0", {"start": v(26.7, -41.08) * mm, "end": v(24.54, -42.4) * mm});
            skLineSegment(sketch, "E29.24.1", {"start": v(28.04, -43.24) * mm, "end": v(26.7, -41.08) * mm});
            skLineSegment(sketch, "E29.24.2", {"start": v(25.87, -44.57) * mm, "end": v(28.04, -43.24) * mm});
            skLineSegment(sketch, "E29.24.3", {"start": v(24.54, -42.4) * mm, "end": v(25.87, -44.57) * mm});
            skLineSegment(sketch, "E29.25.0", {"start": v(32.8, -36.4) * mm, "end": v(30.87, -38.05) * mm});
            skLineSegment(sketch, "E29.25.1", {"start": v(34.46, -38.33) * mm, "end": v(32.8, -36.4) * mm});
            skLineSegment(sketch, "E29.25.2", {"start": v(32.53, -39.98) * mm, "end": v(34.46, -38.33) * mm});
            skLineSegment(sketch, "E29.25.3", {"start": v(30.87, -38.05) * mm, "end": v(32.53, -39.98) * mm});
            skLineSegment(sketch, "E29.26.0", {"start": v(38.1, -30.82) * mm, "end": v(36.45, -32.75) * mm});
            skLineSegment(sketch, "E29.26.1", {"start": v(40.03, -32.46) * mm, "end": v(38.1, -30.82) * mm});
            skLineSegment(sketch, "E29.26.2", {"start": v(38.38, -34.4) * mm, "end": v(40.03, -32.46) * mm});
            skLineSegment(sketch, "E29.26.3", {"start": v(36.45, -32.75) * mm, "end": v(38.38, -34.4) * mm});
            skLineSegment(sketch, "E29.27.0", {"start": v(42.45, -24.48) * mm, "end": v(41.12, -26.64) * mm});
            skLineSegment(sketch, "E29.27.1", {"start": v(44.61, -25.8) * mm, "end": v(42.45, -24.48) * mm});
            skLineSegment(sketch, "E29.27.2", {"start": v(43.29, -27.97) * mm, "end": v(44.61, -25.8) * mm});
            skLineSegment(sketch, "E29.27.3", {"start": v(41.12, -26.64) * mm, "end": v(43.29, -27.97) * mm});
            skLineSegment(sketch, "E29.28.0", {"start": v(45.75, -17.54) * mm, "end": v(44.78, -19.88) * mm});
            skLineSegment(sketch, "E29.28.1", {"start": v(48.1, -18.5) * mm, "end": v(45.75, -17.54) * mm});
            skLineSegment(sketch, "E29.28.2", {"start": v(47.13, -20.85) * mm, "end": v(48.1, -18.5) * mm});
            skLineSegment(sketch, "E29.28.3", {"start": v(44.78, -19.88) * mm, "end": v(47.13, -20.85) * mm});
            skLineSegment(sketch, "E29.29.0", {"start": v(47.93, -10.16) * mm, "end": v(47.34, -12.63) * mm});
            skLineSegment(sketch, "E29.29.1", {"start": v(50.4, -10.75) * mm, "end": v(47.93, -10.16) * mm});
            skLineSegment(sketch, "E29.29.2", {"start": v(49.81, -13.22) * mm, "end": v(50.4, -10.75) * mm});
            skLineSegment(sketch, "E29.29.3", {"start": v(47.34, -12.63) * mm, "end": v(49.81, -13.22) * mm});
            skLineSegment(sketch, "E29.30.0", {"start": v(48.93, -2.54) * mm, "end": v(48.73, -5.07) * mm});
            skLineSegment(sketch, "E29.30.1", {"start": v(51.46, -2.74) * mm, "end": v(48.93, -2.54) * mm});
            skLineSegment(sketch, "E29.30.2", {"start": v(51.27, -5.27) * mm, "end": v(51.46, -2.74) * mm});
            skLineSegment(sketch, "E29.30.3", {"start": v(48.73, -5.07) * mm, "end": v(51.27, -5.27) * mm});
            skLineSegment(sketch, "E29.31.0", {"start": v(48.73, 5.15) * mm, "end": v(48.93, 2.61) * mm});
            skLineSegment(sketch, "E29.31.1", {"start": v(51.26, 5.35) * mm, "end": v(48.73, 5.15) * mm});
            skLineSegment(sketch, "E29.31.2", {"start": v(51.46, 2.82) * mm, "end": v(51.26, 5.35) * mm});
            skLineSegment(sketch, "E29.31.3", {"start": v(48.93, 2.61) * mm, "end": v(51.46, 2.82) * mm});
            skLineSegment(sketch, "E29.32.0", {"start": v(47.32, 12.7) * mm, "end": v(47.92, 10.24) * mm});
            skLineSegment(sketch, "E29.32.1", {"start": v(49.8, 13.3) * mm, "end": v(47.32, 12.7) * mm});
            skLineSegment(sketch, "E29.32.2", {"start": v(50.39, 10.83) * mm, "end": v(49.8, 13.3) * mm});
            skLineSegment(sketch, "E29.32.3", {"start": v(47.92, 10.24) * mm, "end": v(50.39, 10.83) * mm});
            skLineSegment(sketch, "E29.33.0", {"start": v(44.75, 19.95) * mm, "end": v(45.73, 17.6) * mm});
            skLineSegment(sketch, "E29.33.1", {"start": v(47.1, 20.93) * mm, "end": v(44.75, 19.95) * mm});
            skLineSegment(sketch, "E29.33.2", {"start": v(48.07, 18.58) * mm, "end": v(47.1, 20.93) * mm});
            skLineSegment(sketch, "E29.33.3", {"start": v(45.73, 17.6) * mm, "end": v(48.07, 18.58) * mm});
            skLineSegment(sketch, "E29.34.0", {"start": v(41.08, 26.7) * mm, "end": v(42.4, 24.54) * mm});
            skLineSegment(sketch, "E29.34.1", {"start": v(43.24, 28.04) * mm, "end": v(41.08, 26.7) * mm});
            skLineSegment(sketch, "E29.34.2", {"start": v(44.57, 25.87) * mm, "end": v(43.24, 28.04) * mm});
            skLineSegment(sketch, "E29.34.3", {"start": v(42.4, 24.54) * mm, "end": v(44.57, 25.87) * mm});
            skLineSegment(sketch, "E29.35.0", {"start": v(36.4, 32.8) * mm, "end": v(38.05, 30.87) * mm});
            skLineSegment(sketch, "E29.35.1", {"start": v(38.33, 34.46) * mm, "end": v(36.4, 32.8) * mm});
            skLineSegment(sketch, "E29.35.2", {"start": v(39.98, 32.53) * mm, "end": v(38.33, 34.46) * mm});
            skLineSegment(sketch, "E29.35.3", {"start": v(38.05, 30.87) * mm, "end": v(39.98, 32.53) * mm});
            skLineSegment(sketch, "E29.36.0", {"start": v(30.82, 38.1) * mm, "end": v(32.75, 36.45) * mm});
            skLineSegment(sketch, "E29.36.1", {"start": v(32.46, 40.03) * mm, "end": v(30.82, 38.1) * mm});
            skLineSegment(sketch, "E29.36.2", {"start": v(34.4, 38.38) * mm, "end": v(32.46, 40.03) * mm});
            skLineSegment(sketch, "E29.36.3", {"start": v(32.75, 36.45) * mm, "end": v(34.4, 38.38) * mm});
            skLineSegment(sketch, "E29.37.0", {"start": v(24.48, 42.45) * mm, "end": v(26.64, 41.12) * mm});
            skLineSegment(sketch, "E29.37.1", {"start": v(25.8, 44.61) * mm, "end": v(24.48, 42.45) * mm});
            skLineSegment(sketch, "E29.37.2", {"start": v(27.97, 43.29) * mm, "end": v(25.8, 44.61) * mm});
            skLineSegment(sketch, "E29.37.3", {"start": v(26.64, 41.12) * mm, "end": v(27.97, 43.29) * mm});
            skLineSegment(sketch, "E29.38.0", {"start": v(17.54, 45.75) * mm, "end": v(19.88, 44.78) * mm});
            skLineSegment(sketch, "E29.38.1", {"start": v(18.5, 48.1) * mm, "end": v(17.54, 45.75) * mm});
            skLineSegment(sketch, "E29.38.2", {"start": v(20.85, 47.13) * mm, "end": v(18.5, 48.1) * mm});
            skLineSegment(sketch, "E29.38.3", {"start": v(19.88, 44.78) * mm, "end": v(20.85, 47.13) * mm});
            skLineSegment(sketch, "E29.39.0", {"start": v(10.16, 47.93) * mm, "end": v(12.63, 47.34) * mm});
            skLineSegment(sketch, "E29.39.1", {"start": v(10.75, 50.4) * mm, "end": v(10.16, 47.93) * mm});
            skLineSegment(sketch, "E29.39.2", {"start": v(13.22, 49.81) * mm, "end": v(10.75, 50.4) * mm});
            skLineSegment(sketch, "E29.39.3", {"start": v(12.63, 47.34) * mm, "end": v(13.22, 49.81) * mm});
            skPoint(sketch, "E29.center", {"position": v(0, 0) * mm});
            skSolve(sketch);
        }
        {
            var Q0;
            Q0 = qSketchRegion(id + "F15", true);
            extrude(context, id + "F16", {"entities" : qUnion([Q0]), "operationType" : NewBodyOperationType.REMOVE, "oppositeDirection" : true, "depth" : 19.05 * mm, "offsetDistance" : 25.4 * mm});
        }
    });
